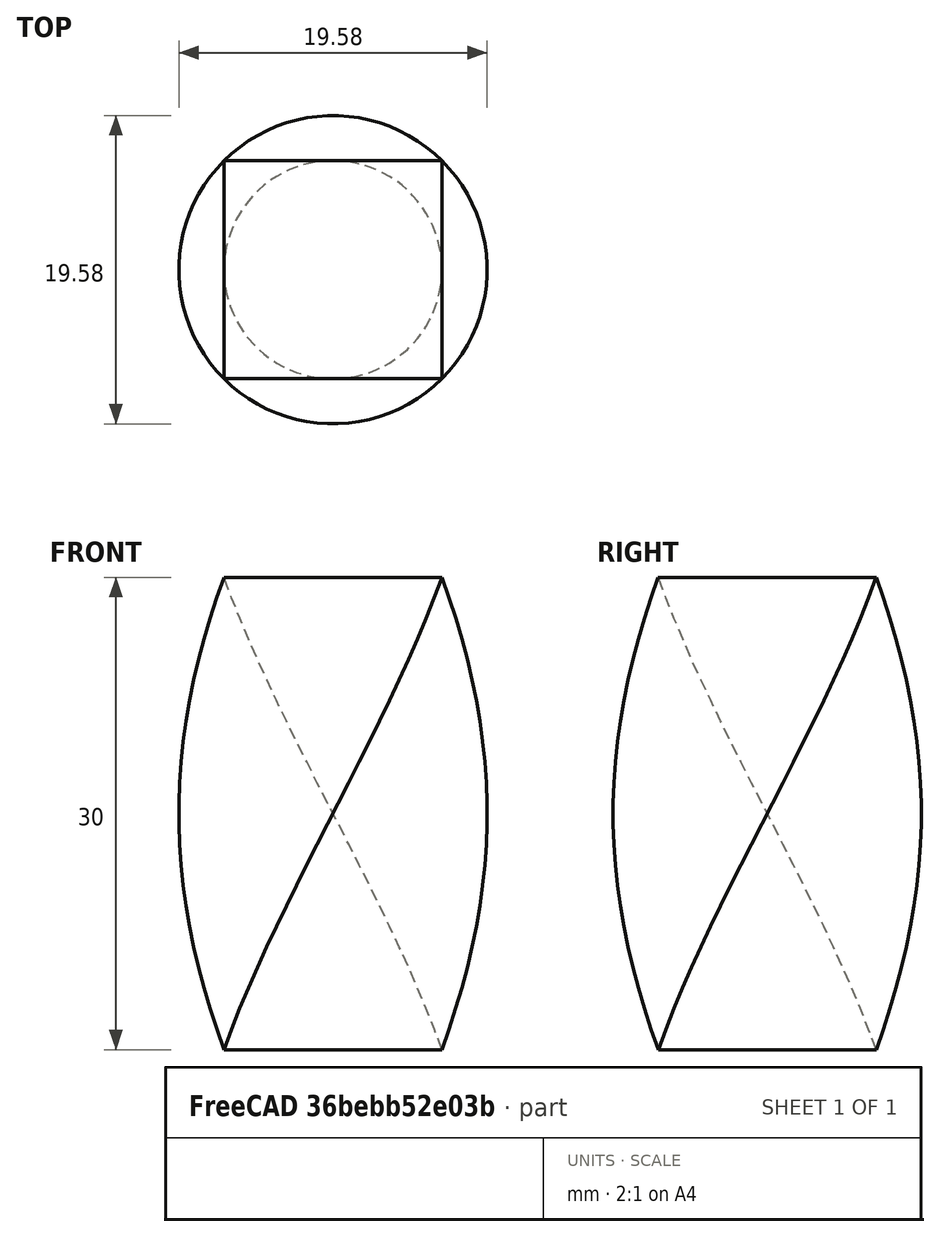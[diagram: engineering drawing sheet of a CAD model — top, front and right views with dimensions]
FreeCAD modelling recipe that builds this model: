
FCSTD DOCUMENT  (FreeCAD 0.17R13217 (Git))
Label: 14-extrusion-tornision
License: All rights reserved
LicenseURL: http://en.wikipedia.org/wiki/All_rights_reserved
objects: Sketcher::SketchObject×1, Part::Helix×1, PartDesign::ShapeBinder×1, PartDesign::AdditivePipe×1, PartDesign::Body×1
note: 6 computed .brp shape members not serialized (recipe doc carries the construction recipe); baked Part::Feature solids carry a one-line shape summary decoded from their .brp

FEATURE [Sketcher::SketchObject] Sketch
  MapMode = 5
  Support = -> [XY_Plane]
  sketch-geometry (4):
    g0: LineSegment StartX=-6.92213 StartY=6.92213 StartZ=0 EndX=6.92213 EndY=6.92213 EndZ=0
    g1: LineSegment StartX=6.92213 StartY=6.92213 StartZ=0 EndX=6.92213 EndY=-6.92213 EndZ=0
    g2: LineSegment StartX=6.92213 StartY=-6.92213 StartZ=0 EndX=-6.92213 EndY=-6.92213 EndZ=0
    g3: LineSegment StartX=-6.92213 StartY=-6.92213 StartZ=0 EndX=-6.92213 EndY=6.92213 EndZ=0
  constraints (10):
    c: Coincident(g0,g1)
    c: Coincident(g1,g2)
    c: Coincident(g2,g3)
    c: Coincident(g3,g0)
    c: Horizontal(g0)
    c: Horizontal(g2)
    c: Vertical(g1)
    c: Vertical(g3)
    c: Symmetric(g0,g1,g-1)
    c: Equal(g3,g0)
FEATURE [Part::Helix] Helix  label="Espiral"
  Angle = 0
  AttacherType = Attacher::AttachEngine3D
  Height = 30
  LocalCoord = 0
  Pitch = 120
  Radius = 1
  Style = 1
FEATURE [PartDesign::ShapeBinder] ReferenceHelix
  Support = -> [Helix]
FEATURE [PartDesign::AdditivePipe] AdditivePipe
  AuxilleryCurvelinear = true
  AuxillerySpineTangent = false
  Binormal = (0,0,0)
  Mode = 2
  Profile = -> Sketch
  Refine = true
  Spine = -> ReferenceHelix
  SpineTangent = false
  Transformation = 0
  Transition = 0
FEATURE [PartDesign::Body] Body
  Group = -> [Sketch,AdditivePipe,ReferenceHelix]
  Origin = -> Origin
  Tip = -> AdditivePipe
